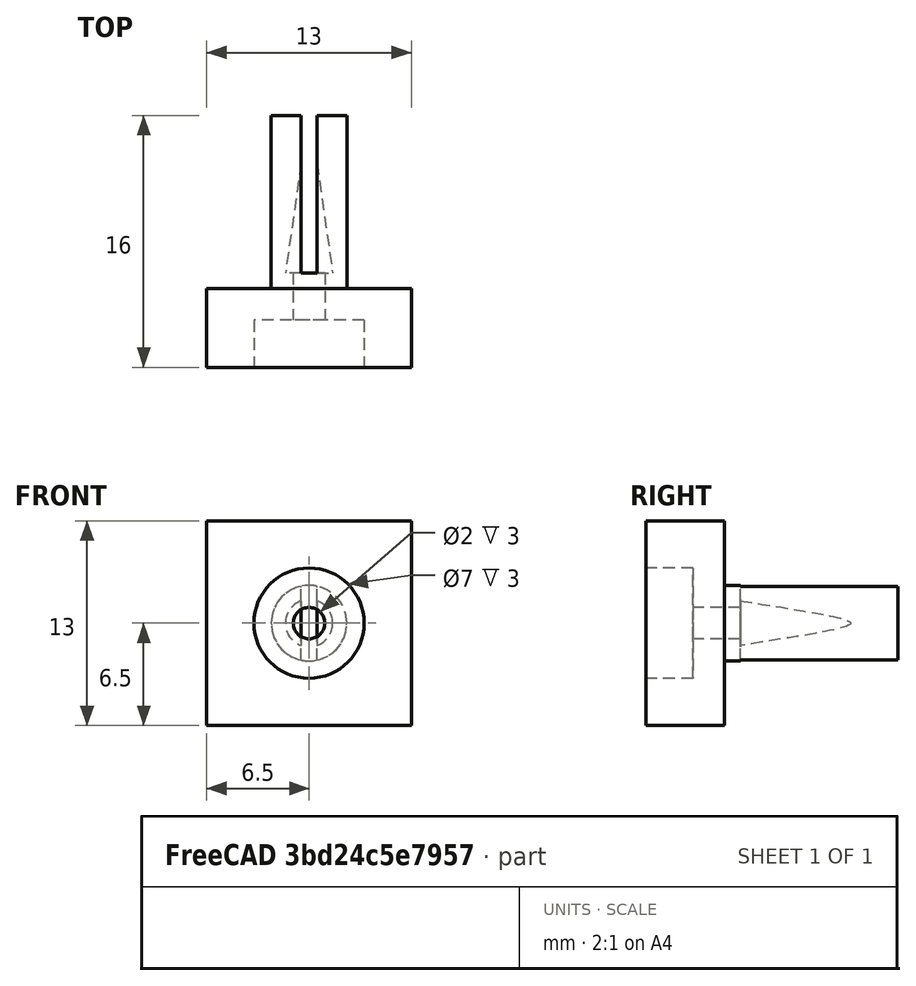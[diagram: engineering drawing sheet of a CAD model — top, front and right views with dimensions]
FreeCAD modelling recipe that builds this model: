
FCSTD DOCUMENT  (FreeCAD 0.16R5560 (Git))
Label: anchor
License: All rights reserved
LicenseURL: http://en.wikipedia.org/wiki/All_rights_reserved
objects: Part::Cylinder×3, Part::Box×2, Part::MultiFuse×2, Part::Cone×1, Part::Cut×1
note: 9 computed .brp shape members not serialized (recipe doc carries the construction recipe); baked Part::Feature solids carry a one-line shape summary decoded from their .brp

FEATURE [Part::Cylinder] Cylinder002  label="anchor pin"
  Angle = 360
  Height = 13
  Placement = pos=(18,72,6) rot=(1,0,0;1.5708rad)
  Radius = 2.4
FEATURE [Part::Box] Box  label="cut"
  Height = 10
  Length = 1
  Placement = pos=(17.5,62,1) rot=(0,0,1;0rad)
  Width = 10
FEATURE [Part::Cone] Cone  label="screw guide"
  Angle = 360
  Height = 7
  Placement = pos=(18,69,6) rot=(1,0,0;1.5708rad)
  Radius1 = 0.5
  Radius2 = 1.5
FEATURE [Part::Cylinder] Cylinder  label="hole"
  Angle = 360
  Height = 3
  Placement = pos=(18,62,6) rot=(1,0,0;1.5708rad)
  Radius = 1
FEATURE [Part::Cylinder] Cylinder005  label="screw head seat"
  Angle = 360
  Height = 3
  Placement = pos=(18,59,6) rot=(1,0,0;1.5708rad)
  Radius = 3.5
FEATURE [Part::MultiFuse] Fusion  label="hole and cut"
  Shapes = -> [Box,Cone,Cylinder,Cylinder005]
FEATURE [Part::Box] Box002  label="squared washer"
  Height = 13
  Length = 13
  Placement = pos=(11.5,56,-0.5) rot=(0,0,1;0rad)
  Width = 5
FEATURE [Part::MultiFuse] Fusion001  label="anchor"
  Shapes = -> [Cylinder002,Box002]
FEATURE [Part::Cut] Cut  label="Anchor with hole and cut"
  Base = -> Fusion001
  Tool = -> Fusion
